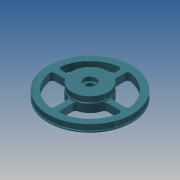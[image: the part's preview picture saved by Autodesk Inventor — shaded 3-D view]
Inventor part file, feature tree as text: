
AUTODESK INVENTOR PART (.ipt)
format: ipt  version: 2013 (Build 170138000, 138)  size: 3,994,624 bytes
history: native  units: mm
features: extrude x4, sketch x4, other x3, fillet x1, pattern_circular x1
ambient origin geometry x8: Origin, YZ Plane, XZ Plane, XY Plane, X Axis, Y Axis, Z Axis, Center Point
bodies: Solid1 (feature_tree)
feature tree (13):
  other  "z idler pulley.iam"
  other  "235 pulley blank.ipt:1"
  other  "100 pulley blank.ipt:1"
  extrude  "Extrusion1"  Depth=15.0mm
  extrude  "Extrusion2"  Depth=22.0mm
  extrude  "Extrusion3"  Depth=7.0mm TaperAngle=0.0deg
  extrude  "Extrusion4"  Depth=5.0mm
  fillet  "Fillet1"  Radius=12.0mm
  pattern_circular  "Circular Pattern1"  [2 undecoded]
  sketch  "Sketch1"  dims[d0=10.0mm d1=15.0mm]
  sketch  "Sketch2"  dims[d3=10.0mm d4=0.0mm d5=22.0mm]
  sketch  "Sketch3"  dims[d7=7.0mm d8=0.0mm d9=7.0mm d10=0.0mm]
  sketch  "Sketch4"  dims[d11=5.0mm d12=5.0mm d13=12.0mm d14=7.0mm d15=0.0mm d16=5.0mm d17=40.0mm d18=360.0deg]
note: 2 required parameter values undecoded (feature->parameter linkage not recoverable at this tier; creation-order binding heuristic only, values carry confidence <= 0.55)
